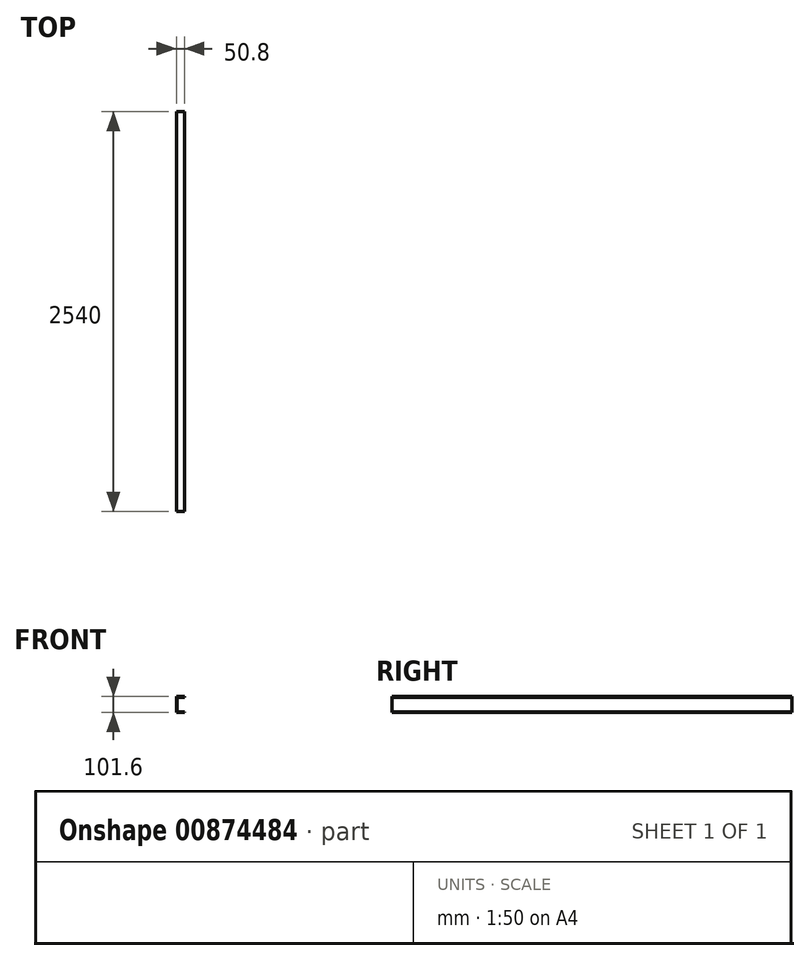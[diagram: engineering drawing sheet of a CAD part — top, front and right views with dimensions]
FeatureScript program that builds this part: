
annotation { "Feature Type Name" : "Feature", "Feature Type Description" : "" }
export const myFeature = defineFeature(function(context is Context, id is Id, definition is map)
    precondition{}
    {
        {
            var Q0;
            Q0=qCreatedBy(makeId("Front.planeOp"),FACE);
            var sketch = newSketch(context, id + "F0", { "sketchPlane" : qUnion([Q0])});
            skLineSegment(sketch, "E0", {"start": v(-8.17, 0) * mm, "end": v(-8.17, 50.8) * mm});
            skLineSegment(sketch, "E1", {"start": v(-8.17, 50.8) * mm, "end": v(42.63, 50.8) * mm});
            skLineSegment(sketch, "E2", {"start": v(42.63, 50.8) * mm, "end": v(42.63, 46.04) * mm});
            skLineSegment(sketch, "E3", {"start": v(42.63, 46.04) * mm, "end": v(-3.41, 46.04) * mm});
            skLineSegment(sketch, "E4", {"start": v(-3.41, 46.04) * mm, "end": v(-3.41, 0) * mm});
            skLineSegment(sketch, "E5.MirrorCS", {"start": v(42.63, -50.8) * mm, "end": v(42.63, -46.04) * mm});
            skLineSegment(sketch, "E6.MirrorCS", {"start": v(-8.17, 0) * mm, "end": v(-8.17, -50.8) * mm});
            skLineSegment(sketch, "E7.MirrorCS", {"start": v(-3.41, -46.04) * mm, "end": v(-3.41, 0) * mm});
            skLineSegment(sketch, "E8.MirrorCS", {"start": v(42.63, -46.04) * mm, "end": v(-3.41, -46.04) * mm});
            skLineSegment(sketch, "E9.MirrorCS", {"start": v(-8.17, -50.8) * mm, "end": v(42.63, -50.8) * mm});
            skSolve(sketch);
        }
        {
            var Q0;
            Q0=makeQuery(id+"F0.imprint","IMPRINT",FACE,{"disambiguationData":[TD([[makeQuery(id+"F0.imprint","IMPRINT",EDGE,{"derivedFrom":sQuery(id+"F0.wireOp",EDGE,"E0")}),-1.0]])]});
            extrude(context, id + "F1", {"entities" : qUnion([Q0]), "oppositeDirection" : true, "depth" : 2540 * mm, "offsetDistance" : 25.4 * mm});
        }
    });
